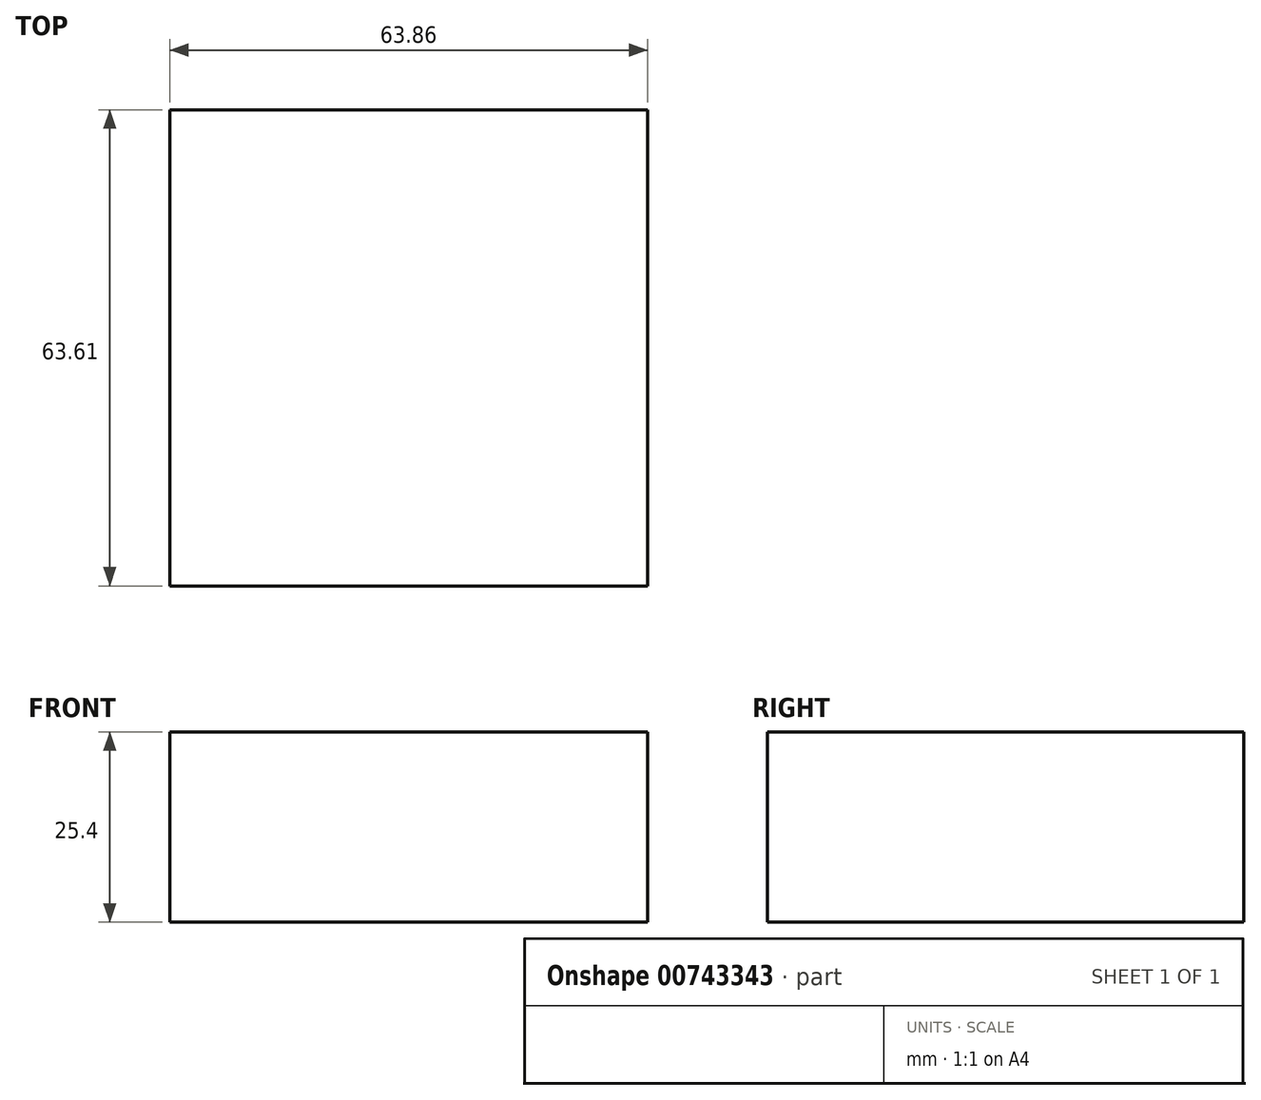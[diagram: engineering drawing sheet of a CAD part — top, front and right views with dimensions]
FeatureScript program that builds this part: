
annotation { "Feature Type Name" : "Feature", "Feature Type Description" : "" }
export const myFeature = defineFeature(function(context is Context, id is Id, definition is map)
    precondition{}
    {
        {
            var Q0;
            Q0=qCreatedBy(makeId("Top.planeOp"),FACE);
            var sketch = newSketch(context, id + "F0", { "sketchPlane" : qUnion([Q0])});
            skLineSegment(sketch, "E0.bottom", {"start": v(-23.92, -28.72) * mm, "end": v(39.94, -28.72) * mm});
            skLineSegment(sketch, "E0.top", {"start": v(-23.92, 34.89) * mm, "end": v(39.94, 34.89) * mm});
            skLineSegment(sketch, "E0.left", {"start": v(-23.92, -28.72) * mm, "end": v(-23.92, 34.89) * mm});
            skLineSegment(sketch, "E0.right", {"start": v(39.94, -28.72) * mm, "end": v(39.94, 34.89) * mm});
            skLineSegment(sketch, "E1.bottom", {"start": v(-4.44, -138.2) * mm, "end": v(-28.85, -138.2) * mm});
            skLineSegment(sketch, "E1.top", {"start": v(-4.44, -131.79) * mm, "end": v(-28.85, -131.79) * mm});
            skLineSegment(sketch, "E1.left", {"start": v(-4.44, -138.2) * mm, "end": v(-4.44, -131.79) * mm});
            skLineSegment(sketch, "E1.right", {"start": v(-28.85, -138.2) * mm, "end": v(-28.85, -131.79) * mm});
            skSolve(sketch);
        }
        {
            var Q0;
            Q0=makeQuery(id+"F0.imprint","IMPRINT",FACE,{"disambiguationData":[TD([[makeQuery(id+"F0.imprint","IMPRINT",EDGE,{"derivedFrom":sQuery(id+"F0.wireOp",EDGE,"E0.bottom")}),1.0]])]});
            extrude(context, id + "F1", {"entities" : qUnion([Q0]), "depth" : 25.4 * mm, "offsetDistance" : 25.4 * mm});
        }
    });
